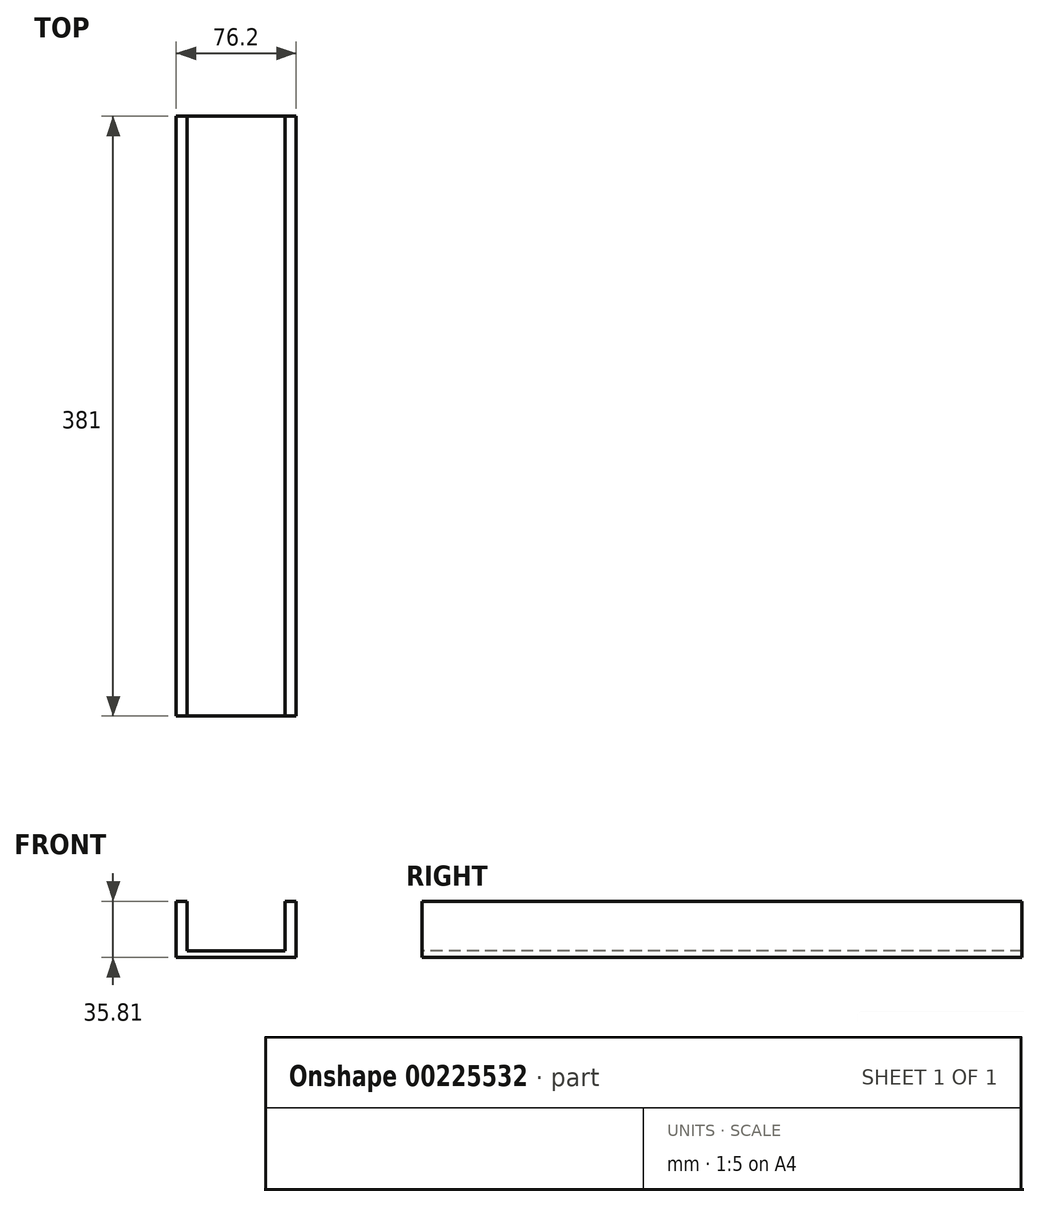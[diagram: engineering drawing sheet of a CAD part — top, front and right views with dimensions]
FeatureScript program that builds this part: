
annotation { "Feature Type Name" : "Feature", "Feature Type Description" : "" }
export const myFeature = defineFeature(function(context is Context, id is Id, definition is map)
    precondition{}
    {
        {
            var Q0;
            Q0=qCreatedBy(makeId("Top.planeOp"),FACE);
            var sketch = newSketch(context, id + "F0", { "sketchPlane" : qUnion([Q0])});
            skLineSegment(sketch, "E0.bottom", {"start": v(-33.58, 274.38) * mm, "end": v(42.62, 274.38) * mm});
            skLineSegment(sketch, "E0.top", {"start": v(-33.58, -106.62) * mm, "end": v(42.62, -106.62) * mm});
            skLineSegment(sketch, "E0.left", {"start": v(-33.58, 274.38) * mm, "end": v(-33.58, -106.62) * mm});
            skLineSegment(sketch, "E0.right", {"start": v(42.62, 274.38) * mm, "end": v(42.62, -106.62) * mm});
            skSolve(sketch);
        }
        {
            var Q0;
            Q0 = qSketchRegion(id + "F0", true);
            extrude(context, id + "F1", {"entities" : qUnion([Q0]), "depth" : 35.81 * mm});
        }
        {
            var Q0;
            Q0=makeQuery(id+"F1.opExtrude","SWEPT_FACE",FACE,{"disambiguationData":[OSD([sQuery(id+"F0.wireOp",EDGE,"E0.top")])]});
            var sketch = newSketch(context, id + "F2", { "sketchPlane" : qUnion([Q0])});
            skLineSegment(sketch, "E1.bottom", {"start": v(-26.65, 35.81) * mm, "end": v(35.69, 35.81) * mm});
            skLineSegment(sketch, "E1.top", {"start": v(-26.65, 4.32) * mm, "end": v(35.69, 4.32) * mm});
            skLineSegment(sketch, "E1.left", {"start": v(-26.65, 35.81) * mm, "end": v(-26.65, 4.32) * mm});
            skLineSegment(sketch, "E1.right", {"start": v(35.69, 35.81) * mm, "end": v(35.69, 4.32) * mm});
            skSolve(sketch);
        }
        {
            var Q0;
            Q0 = qSketchRegion(id + "F2", true);
            extrude(context, id + "F3", {"entities" : qUnion([Q0]), "operationType" : NewBodyOperationType.REMOVE, "endBound" : BoundingType.THROUGH_ALL, "oppositeDirection" : true, "depth" : 25.4 * mm});
        }
    });
